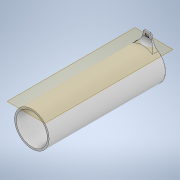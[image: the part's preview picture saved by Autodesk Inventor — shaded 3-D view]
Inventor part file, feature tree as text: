
AUTODESK INVENTOR PART (.ipt)
format: ipt  version: 2021 (Build 250183000, 183)  size: 361,472 bytes
history: native  units: in
note: dims shown in document units (in); Inventor stores cm internally (conversion verified against a paired STEP export)
features: sketch x7, extrude x6, projected_geometry x6, fillet x5, pattern_linear x2, hole x1, plane x1
ambient origin geometry x8: Origin, YZ Plane, XZ Plane, XY Plane, X Axis, Y Axis, Z Axis, Center Point
bodies: Solid1 (feature_tree)
feature tree (28):
  extrude  "Extrusion1"  Depth=5.9055in TaperAngle=0.0deg
  hole  "Hole1"  [1 undecoded]
  plane  "Work Plane1"
  extrude  "Extrusion2"  Depth=0.4724in TaperAngle=0.0deg
  fillet  "Fillet1"  Radius=0.0394in
  extrude  "Extrusion3"  Depth=0.0157in
  extrude  "Extrusion4"  Depth=0.0787in TaperAngle=0.0deg
  fillet  "Fillet2"  Radius=0.1929in
  fillet  "Fillet3"  Radius=0.122in
  fillet  "Fillet4"  Radius=0.1004in
  fillet  "Fillet5"  Radius=0.0984in
  extrude  "Extrusion5"  TaperAngle=0.0deg  [1 undecoded]
  pattern_linear  "Rectangular Pattern1"  Spacing1=0.0591in  [1 undecoded]
  extrude  "Extrusion6"  Depth=0.0394in
  pattern_linear  "Rectangular Pattern2"  Spacing1=0.7087in  [1 undecoded]
  sketch  "Sketch2"  dims[d2=1.752in d3=5.9055in d4=0.0in]
  sketch  "Sketch3"  dims[d5=1.378in]
  projected_geometry  "Projected Loop1"
  sketch  "Sketch4"  dims[d6=1.5748in d7=3.3in d8=0.3125in d9=0.164in d10=0.5635in d11=5.4134in d12=0.8108in d13=0.3937in]
  projected_geometry  "Projected Loop2"
  sketch  "Sketch5"  dims[d14=0.0551in d15=0.4724in d16=0.0in]
  projected_geometry  "Projected Loop3"
  projected_geometry  "Projected Loop4"
  sketch  "Sketch6"  dims[d17=0.0295in d18=0.0in d19=0.2362in d20=0.0394in]
  sketch  "Sketch7"  dims[d21=0.0157in d22=0.0157in]
  projected_geometry  "Projected Loop5"
  sketch  "Sketch8"  dims[d23=0.377in d24=0.0in d25=0.9697in d26=0.0in d27=0.1929in d28=0.122in d29=0.1004in d30=0.0984in d31=0.0in d32=0.0in d33=0.0591in d34=0.0394in d35=0.7087in d36=0.0217in d37=0.0157in d38=0.0157in d39=0.9395in d40=0.0in d41=2.7559in d43=0.0394in d44=2.7559in d46=0.1575in d47=0.0197in d48=1.9685in d49=0.0059in d50=0.0in d51=9.0551in d53=0.0787in]
  projected_geometry  "Projected Loop6"
note: 4 required parameter values undecoded (feature->parameter linkage not recoverable at this tier; creation-order binding heuristic only, values carry confidence <= 0.55)
